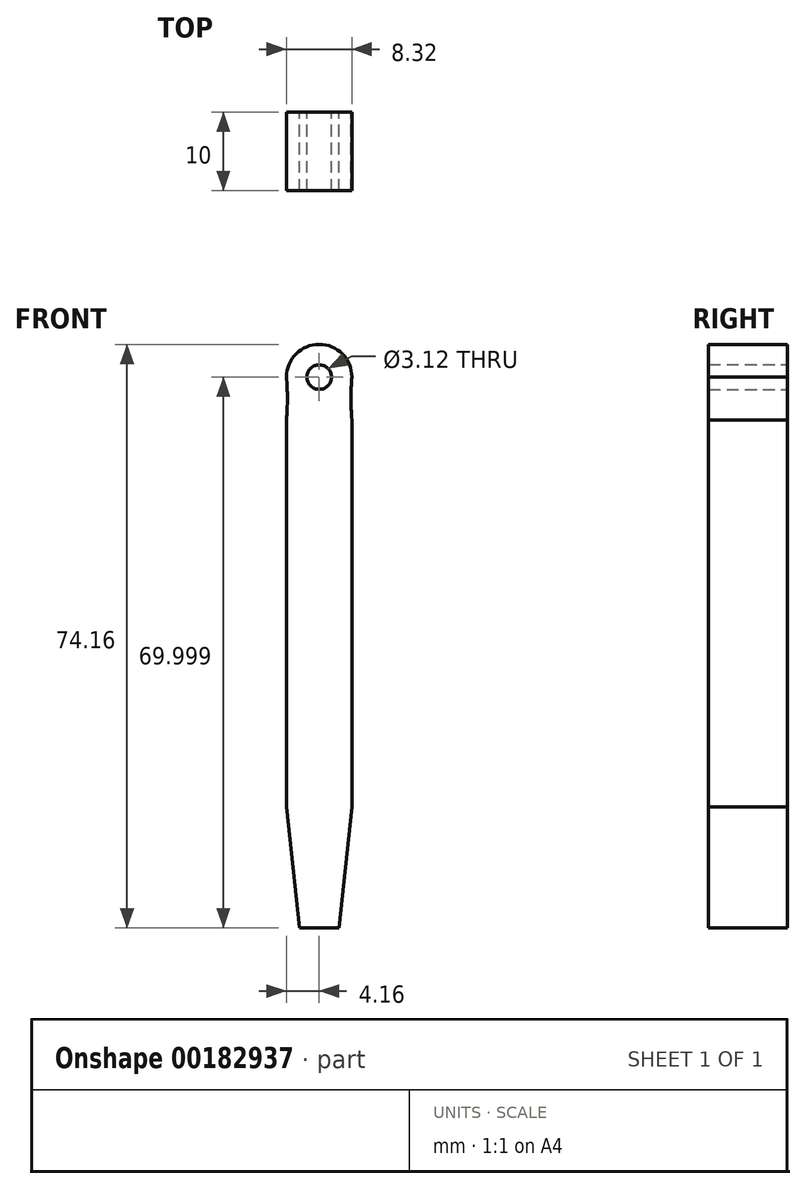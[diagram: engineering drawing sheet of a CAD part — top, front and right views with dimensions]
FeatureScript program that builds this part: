
annotation { "Feature Type Name" : "Feature", "Feature Type Description" : "" }
export const myFeature = defineFeature(function(context is Context, id is Id, definition is map)
    precondition{}
    {
        {
            var Q0;
            Q0=qCreatedBy(makeId("Front.planeOp"),FACE);
            var sketch = newSketch(context, id + "F0", { "sketchPlane" : qUnion([Q0])});
            skLineSegment(sketch, "E0.left", {"start": v(-4.16, 19.18) * mm, "end": v(-4.16, -30) * mm});
            skLineSegment(sketch, "E0.right", {"start": v(4.16, 15.62) * mm, "end": v(4.16, -30) * mm});
            skArc(sketch, "E1", {"start": v(-4.16, 19.18) * mm, "mid": v(-4.03, 21.9) * mm, "end": v(-4.16, 24.6) * mm});
            skArc(sketch, "E2", {"start": v(4.16, 24.6) * mm, "mid": v(0, 28.77) * mm, "end": v(-4.16, 24.6) * mm});
            skArc(sketch, "E3.MirrorCS", {"start": v(4.16, 19.18) * mm, "mid": v(4.03, 21.9) * mm, "end": v(4.16, 24.6) * mm});
            skLineSegment(sketch, "E4", {"start": v(-2.5, -45.4) * mm, "end": v(2.5, -45.4) * mm});
            skCircle(sketch, "E5", {"center": v(0, 24.6) * mm, "radius": 1.56 * mm});
            skLineSegment(sketch, "E6", {"start": v(-4.16, -30) * mm, "end": v(-2.5, -45.4) * mm});
            skLineSegment(sketch, "E7", {"start": v(4.16, -30) * mm, "end": v(2.5, -45.4) * mm});
            skLineSegment(sketch, "E8", {"start": v(4.16, 19.18) * mm, "end": v(4.16, 15.62) * mm});
            skSolve(sketch);
        }
        {
            var Q0;
            Q0=makeQuery(id+"F0.imprint","IMPRINT",FACE,{"disambiguationData":[TD([[makeQuery(id+"F0.imprint","IMPRINT",EDGE,{"derivedFrom":sQuery(id+"F0.wireOp",EDGE,"E0.left")}),1.0]])]});
            var Q1;
            Q1=makeQuery(id+"F0.imprint","IMPRINT",FACE,{"disambiguationData":[TD([[makeQuery(id+"F0.imprint","IMPRINT",EDGE,{"derivedFrom":sQuery(id+"F0.wireOp",EDGE,"E4")}),1.0]])]});
            extrude(context, id + "F1", {"entities" : qUnion([Q0, Q1]), "depth" : 10 * mm});
        }
    });
